# Revit family: Forno New Inox Basic 60
name_source: partatom
category: Modelos genéricos
units: mm (PartAtom-declared; Revit-internal decimal feet)

## family parameters
Com base no plano de trabalho = Não
Compartilhado = Não
Corte com vazios quando carregada = Não
Cota do conector redondo = Utilizar diâmetro
Pode hospedar o vergalhão = Não
Ponto de cálculo do ambiente = Não
Sempre na vertical = Sim
Tipo de parte = Normal

## types (1)
- Forno New Inox Basic 60
    Acabamento = Escovado
    Acessórios inclusos = Bandeja e grelha
    Aço inox com tratamento anti-digitais" = Sim
    Capacidade = 70 L
    Descrição = Forno Elétrico
    Dimensões = 595 x 595 x 575 mm (Profundidade)
    Elevação padrão = 0 mm  [stored 0 ft]
    Fabricante = Tramontina
    Frequência = 50 - 60 Hz
    Funções = 3
    Lâmpada para iluminação interna = Sim
    Material predominante = Aço Inox
    Modelo = Forno Elétrico Inox Basic 60 F3
    Posições para grelhas e bandejas = 5
    Potência inferior = 1000 W
    Potência superior = 1150 W
    Potência total = 2150 W
    Referência do produto = 94864/222
    Temperatura máxima interna = 250 °C
    Tensão = 220 V
    Timer com desligamento automático = Sim
    Tipo de material = AISI 304
    URL da ficha técnica = https://assets.tramontina.com.br
    URL do fabricante = tramontina.com.br
    URL do produto = https://www.tramontina.com.br
    URL dos arquivos BIM = tramontina.com.br/biblioteca

note: [stored X ft] marks values corroborated as IEEE doubles in the binary element streams (Revit-internal decimal feet)
